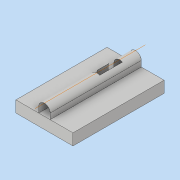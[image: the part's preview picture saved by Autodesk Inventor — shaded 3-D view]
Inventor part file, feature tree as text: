
AUTODESK INVENTOR PART (.ipt)
format: ipt  version: 2019 (Build 230136000, 136)  size: 144,384 bytes
history: native  units: mm
features: other x3, extrude x3, projected_geometry x1
ambient origin geometry x8: Origin, YZ Plane, XZ Plane, XY Plane, X Axis, Y Axis, Z Axis, Center Point
bodies: Body1 (feature_tree)
feature tree (7):
  other  "эскиз_корпус"
  extrude  "корпус_общий"  Depth=5.0mm
  extrude  "отверстие_ручка"  Depth=5.0mm
  extrude  "отверстие_цилиндр"  Depth=0.05mm
  other  "РабОсь1"
  other  "эскиз_отверстие_ручка"
  projected_geometry  "Спроецированная петля6"
